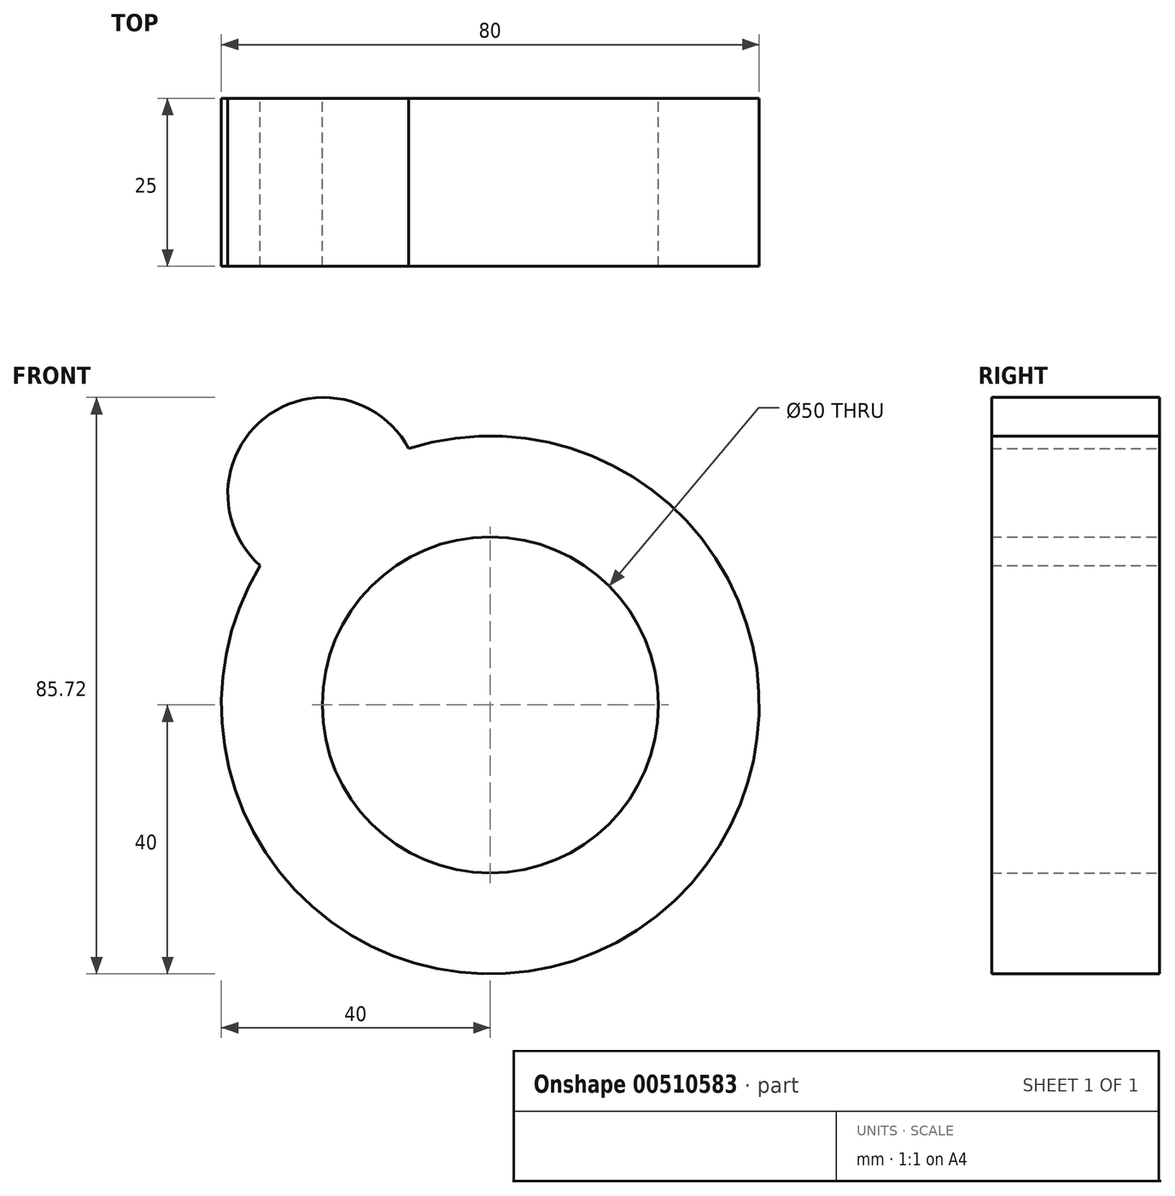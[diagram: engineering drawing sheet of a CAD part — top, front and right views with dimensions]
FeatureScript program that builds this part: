
annotation { "Feature Type Name" : "Feature", "Feature Type Description" : "" }
export const myFeature = defineFeature(function(context is Context, id is Id, definition is map)
    precondition{}
    {
        {
            var Q0;
            Q0=qCreatedBy(makeId("Front.planeOp"),FACE);
            var sketch = newSketch(context, id + "F0", { "sketchPlane" : qUnion([Q0])});
            skCircle(sketch, "E0", {"center": v(0, 0) * mm, "radius": 2.5 * mm});
            skCircle(sketch, "E1", {"center": v(0, 0) * mm, "radius": 8 * mm});
            skCircle(sketch, "E2", {"center": v(0, 0) * mm, "radius": 25 * mm});
            skCircle(sketch, "E3", {"center": v(0, 0) * mm, "radius": 40 * mm});
            skCircle(sketch, "E4", {"center": v(-24.75, 31.42) * mm, "radius": 14.3 * mm});
            skSolve(sketch);
        }
        {
            var Q0;
            Q0 = qSketchRegion(id + "F0", true);
            extrude(context, id + "F1", {"entities" : qUnion([Q0]), "depth" : 25 * mm, "offsetDistance" : 25 * mm});
        }
    });
